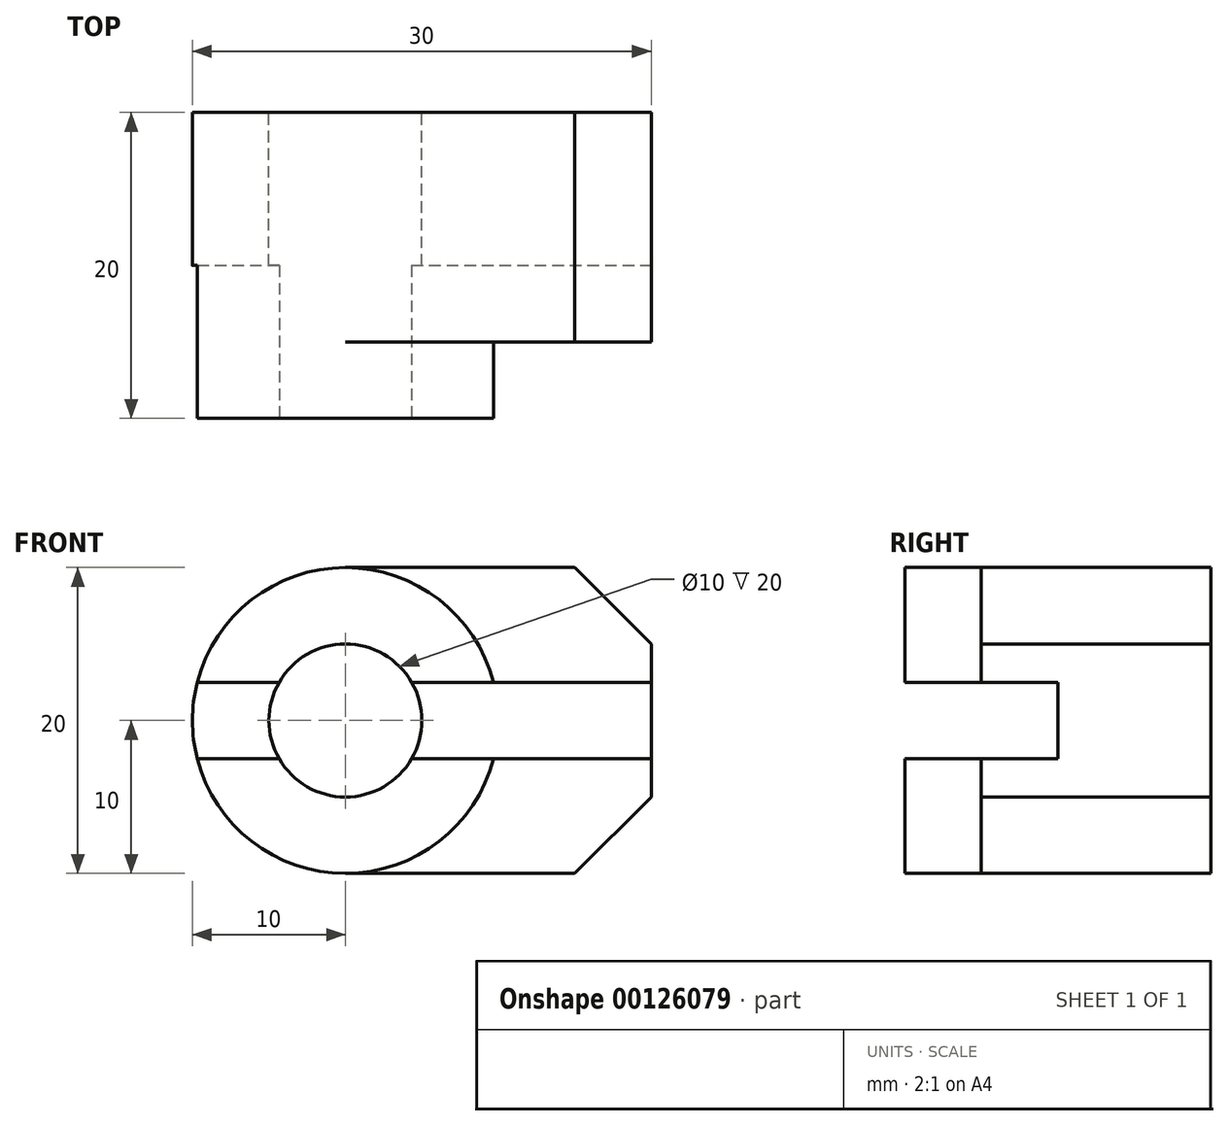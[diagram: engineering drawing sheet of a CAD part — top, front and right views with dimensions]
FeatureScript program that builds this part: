
annotation { "Feature Type Name" : "Feature", "Feature Type Description" : "" }
export const myFeature = defineFeature(function(context is Context, id is Id, definition is map)
    precondition{}
    {
        {
            var Q0;
            Q0=qCreatedBy(makeId("Front.planeOp"),FACE);
            var sketch = newSketch(context, id + "F0", { "sketchPlane" : qUnion([Q0])});
            skCircle(sketch, "E0", {"center": v(0, 0) * mm, "radius": 10 * mm});
            skLineSegment(sketch, "E1", {"start": v(0, 10) * mm, "end": v(15, 10) * mm});
            skLineSegment(sketch, "E2", {"start": v(15, 10) * mm, "end": v(20, 5) * mm});
            skLineSegment(sketch, "E3", {"start": v(20, 5) * mm, "end": v(20, -5) * mm});
            skLineSegment(sketch, "E4", {"start": v(20, -5) * mm, "end": v(15, -10) * mm});
            skLineSegment(sketch, "E5", {"start": v(15, -10) * mm, "end": v(0, -10) * mm});
            skCircle(sketch, "E6", {"center": v(0, 0) * mm, "radius": 5 * mm});
            skSolve(sketch);
        }
        {
            var Q0;
            {var subQ0=sQuery(id+"F0.wireOp",EDGE,"E1");Q0=makeQuery(id+"F0.imprint","IMPRINT",FACE,{"disambiguationData":[TD([[makeQuery(id+"F0.imprint","IMPRINT",EDGE,{"derivedFrom":subQ0}),-1.0]])]});}
            extrude(context, id + "F1", {"entities" : qUnion([Q0]), "depth" : 15 * mm});
        }
        {
            var Q0;
            Q0=makeQuery(id+"F0.imprint","IMPRINT",FACE,{"disambiguationData":[TD([[makeQuery(id+"F0.imprint","IMPRINT",EDGE,{"derivedFrom":sQuery(id+"F0.wireOp",EDGE,"E6")}),-1.0]])]});
            extrude(context, id + "F2", {"entities" : qUnion([Q0]), "operationType" : NewBodyOperationType.ADD, "depth" : 20 * mm});
        }
        {
            var Q0;
            Q0=makeQuery(id+"F2.opExtrude","CAP_FACE",FACE,{"disambiguationData":[OSD([sQuery(id+"F0.wireOp",EDGE,"E0"),sQuery(id+"F0.wireOp",EDGE,"E6")])],"isStart":false});
            var sketch = newSketch(context, id + "F3", { "sketchPlane" : qUnion([Q0])});
            skLineSegment(sketch, "E7", {"start": v(-10, 2.5) * mm, "end": v(20, 2.5) * mm});
            skLineSegment(sketch, "E8", {"start": v(20, 2.5) * mm, "end": v(20, 0) * mm});
            skLineSegment(sketch, "E9", {"start": v(-10, 2.5) * mm, "end": v(-10, 0) * mm});
            skLineSegment(sketch, "E10.MirrorCS", {"start": v(-10, -2.5) * mm, "end": v(-10, 0) * mm});
            skLineSegment(sketch, "E11.MirrorCS", {"start": v(-10, -2.5) * mm, "end": v(20, -2.5) * mm});
            skLineSegment(sketch, "E12.MirrorCS", {"start": v(20, -2.5) * mm, "end": v(20, 0) * mm});
            skSolve(sketch);
        }
        {
            var Q0;
            {var subQ0=makeQuery(id+"F2.opExtrude","CAP_EDGE",EDGE,{"disambiguationData":[OSD([sQuery(id+"F0.wireOp",EDGE,"E0")])],"isStart":false});var subQ2=sQuery(id+"F3.wireOp",EDGE,"E7");var subQ3=makeQuery(id+"F3.imprint","INTERSECT",VERTEX,{"disambiguationData":[OD(0.0)],"derivedFrom":[subQ0,subQ2]});Q0=makeQuery(id+"F3.imprint","IMPRINT",FACE,{"disambiguationData":[TD([[makeQuery(id+"F3.imprint","IMPRINT",EDGE,{"disambiguationData":[TD([[subQ3,-1.0]])],"derivedFrom":subQ2}),-1.0]])]});}
            var Q1;
            {var subQ0=sQuery(id+"F3.wireOp",EDGE,"E7");var subQ1=makeQuery(id+"F2.opExtrude","CAP_EDGE",EDGE,{"disambiguationData":[OSD([sQuery(id+"F0.wireOp",EDGE,"E0")])],"isStart":false});var subQ2=makeQuery(id+"F3.imprint","INTERSECT",VERTEX,{"disambiguationData":[OD(1.0)],"derivedFrom":[subQ1,subQ0]});Q1=makeQuery(id+"F3.imprint","IMPRINT",FACE,{"disambiguationData":[TD([[makeQuery(id+"F3.imprint","IMPRINT",EDGE,{"disambiguationData":[TD([[subQ2,1.0]])],"derivedFrom":subQ0}),-1.0]])]});}
            var Q2;
            {var subQ4=sQuery(id+"F3.wireOp",EDGE,"E8");Q2=makeQuery(id+"F3.imprint","IMPRINT",FACE,{"disambiguationData":[TD([[makeQuery(id+"F3.imprint","IMPRINT",EDGE,{"derivedFrom":subQ4}),-1.0]])]});}
            extrude(context, id + "F4", {"entities" : qUnion([Q0, Q1, Q2]), "operationType" : NewBodyOperationType.REMOVE, "oppositeDirection" : true, "depth" : 10 * mm});
        }
    });
